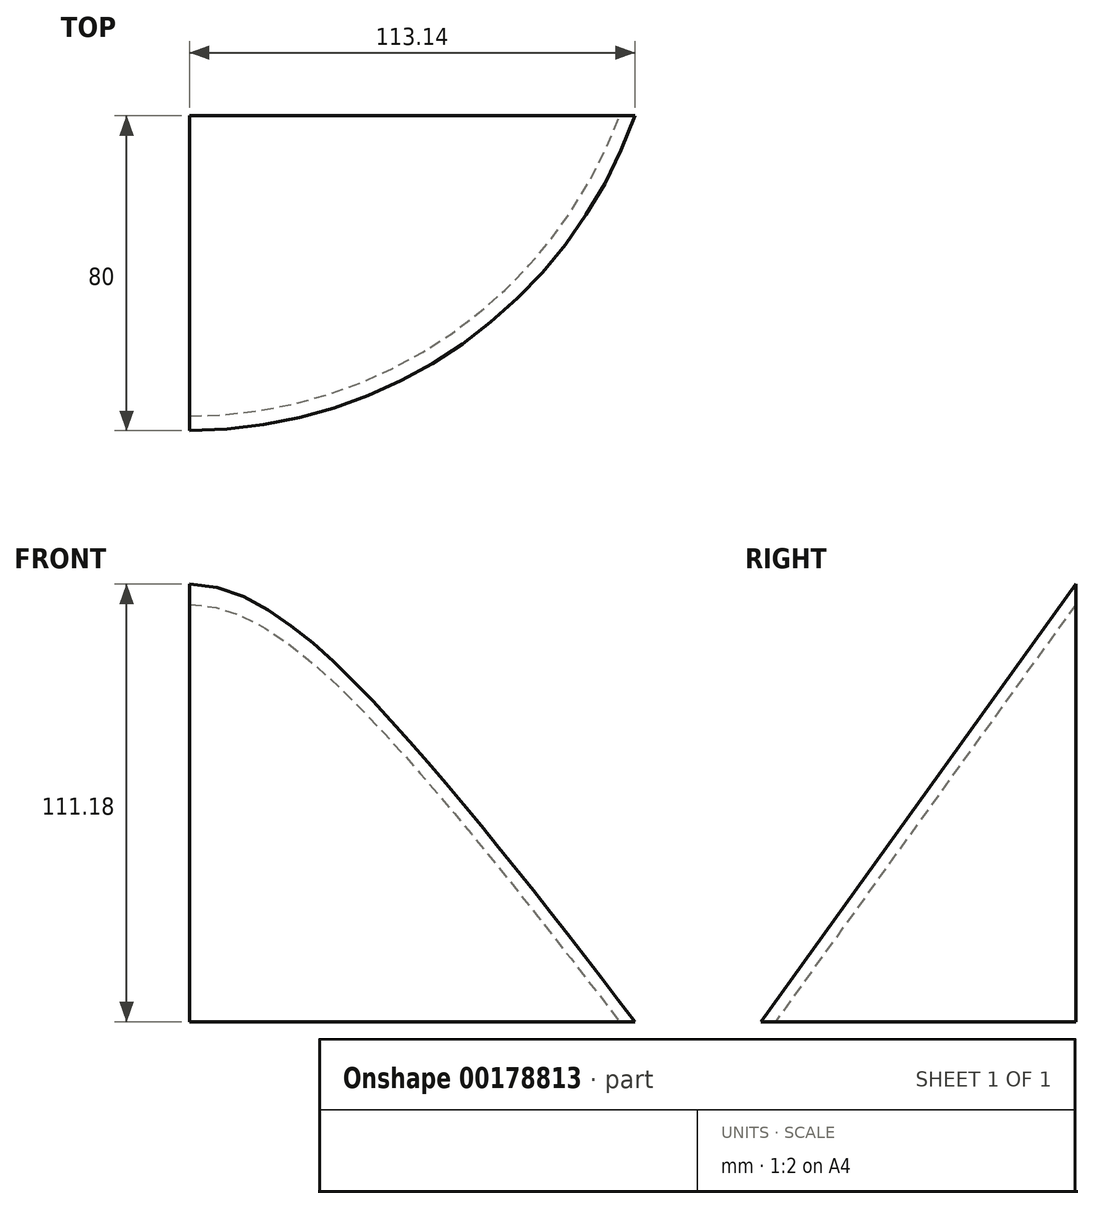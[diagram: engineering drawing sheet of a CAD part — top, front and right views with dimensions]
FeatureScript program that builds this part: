
annotation { "Feature Type Name" : "Feature", "Feature Type Description" : "" }
export const myFeature = defineFeature(function(context is Context, id is Id, definition is map)
    precondition{}
    {
        {
            var Q0;
            Q0=qCreatedBy(makeId("Right.planeOp"),FACE);
            var sketch = newSketch(context, id + "F0", { "sketchPlane" : qUnion([Q0])});
            skLineSegment(sketch, "E0", {"start": v(0, 111.18) * mm, "end": v(0, -68.82) * mm});
            skLineSegment(sketch, "E1", {"start": v(0, 0) * mm, "end": v(-80, 0) * mm});
            skLineSegment(sketch, "E2", {"start": v(0, 111.18) * mm, "end": v(-80, 0) * mm});
            skLineSegment(sketch, "E3", {"start": v(0, 0) * mm, "end": v(40, 0) * mm});
            skLineSegment(sketch, "E4", {"start": v(40, 0) * mm, "end": v(40, 68.08) * mm});
            skLineSegment(sketch, "E5", {"start": v(-80, 0) * mm, "end": v(-77.56, -1.75) * mm});
            skLineSegment(sketch, "E6", {"start": v(0, 111.18) * mm, "end": v(2.44, 109.42) * mm});
            skLineSegment(sketch, "E7", {"start": v(2.44, 109.42) * mm, "end": v(-77.56, -1.75) * mm});
            skSolve(sketch);
        }
        {
            var Q0;
            {var subQ0=sQuery(id+"F0.wireOp",EDGE,"E2");Q0=makeQuery(id+"F0.imprint","IMPRINT",FACE,{"disambiguationData":[TD([[makeQuery(id+"F0.imprint","IMPRINT",EDGE,{"derivedFrom":subQ0}),1.0]])]});}
            var Q1;
            Q1=sQuery(id+"F0.wireOp",EDGE,"E4");
            revolve(context, id + "F1", {"entities" : qUnion([Q0]), "axis" : qUnion([Q1]), "revolveType" : RevolveType.ONE_DIRECTION, "angle" : 100 * degree});
        }
        {
            var Q0;
            Q0=qCreatedBy(makeId("Top.planeOp"),FACE);
            var sketch = newSketch(context, id + "F2", { "sketchPlane" : qUnion([Q0])});
            skLineSegment(sketch, "E8.bottom", {"start": v(0, 0) * mm, "end": v(125.23, 0) * mm});
            skLineSegment(sketch, "E8.top", {"start": v(0, 72.21) * mm, "end": v(125.23, 72.21) * mm});
            skLineSegment(sketch, "E8.left", {"start": v(0, 0) * mm, "end": v(0, 72.21) * mm});
            skLineSegment(sketch, "E8.right", {"start": v(125.23, 0) * mm, "end": v(125.23, 72.21) * mm});
            skSolve(sketch);
        }
        {
            var Q0;
            Q0=makeQuery(id+"F2.imprint","IMPRINT",FACE,{"disambiguationData":[TD([[makeQuery(id+"F2.imprint","IMPRINT",EDGE,{"derivedFrom":sQuery(id+"F2.wireOp",EDGE,"E8.bottom")}),1.0]])]});
            extrude(context, id + "F3", {"entities" : qUnion([Q0]), "operationType" : NewBodyOperationType.REMOVE, "depth" : 200 * mm});
        }
    });
